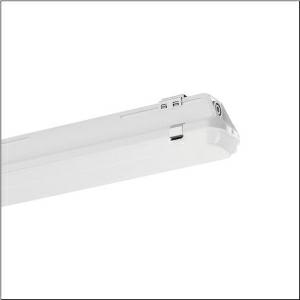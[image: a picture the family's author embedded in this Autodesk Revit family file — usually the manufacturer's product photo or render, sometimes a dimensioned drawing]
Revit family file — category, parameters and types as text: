
# Revit family: monsun_r__11_51fp107p430h_5718
name_source: partatom
category: Lighting Fixtures
units: mm (PartAtom-declared; Revit-internal decimal feet)

## family parameters
Cut with Voids When Loaded = No
Host = Face
Light Source = No
Part Type = Normal
Room Calculation Point = No
Round Connector Dimension = Use Diameter
Shared = No

## types (1)
- Monsun® 11 (1 x LED, 3970 lm, 22.2 W, 4000K)
    Apparent Load = 22 VA
    CIE Flux Codes = 47 77 93 94 100
    Color Rendering = 80
    Color Temperature = 4000K
    Default Elevation = 1800 mm
    Description = Monsun® 11, damp-proof luminaire, chain hanger, primary optical cover: enclosure, of PMMA, light emission: direct distribution, primary light characteristic: symmetric, installation type: suspended mounting, surface-mounted, horizontal mounting, vertical mounting, LED, rated luminous flux: 3.970lm, luminous efficacy: 179lm/W, light colour: 840, colour temperature: 4000K, control gear: ON/OFF, with terminal, 3-pole, max. 2.5mm², mains connection: 220..240V, AC, 50/60Hz, rated input power: 22W, luminaire housing, of glass-fibre reinforced polyester, uncoated, bright grey, incl. chain hanger, length: 1.590mm, width: 90mm, height: 88mm, clip for enclosure, of stainless steel (V2A), ceiling mounting element, of stainless steel (V2A), chain hanger, of stainless steel (V2A), protection rating (complete): IP66, insulation class (complete): insulation class I (protective earthing), certification: CE, ENEC, VDE, UKCA, protection symbol: D, impact resistance: IK04, permissible operating ambient temperature: -35..+40°C, standard: EN 50419, EN 60598-2-1, no direct snow, no direct sun, no direct rain, for indoor or canopied outdoor use, corresponds to IFS (International Featured Standards) requirements for safety and quality in the food industry, contact your sales advisor before using the luminaires in applications with unclear chemical exposure, large temperature fluctuations or condensation-forming humidity, LABS conformity tested according to VDMA 24364:2018-05, packaging unit: 1 piece
    Height = 89 mm
    Lamp = 1 x LED
    Lamp Light Flux = 3970 lm
    Lamp Power = 22.2 W
    Lamp count = 1
    Length = 1590 mm
    Luminous efficacy = 179 lm/W
    Manufacturer = Siteco
    ModVariant = No
    Model = 51FP107P430H
    Mounting Place = Ceiling
    Mounting Type = Surface mounted
    Number of Poles = 1
    OnlyDefault = Yes
    Power Factor = 1
    Product Name = Monsun® 11
    Product group = damp-proof luminaire
    ProductGroupID = 301
    Protection Class = Protection class I
    Protection Degree = IP 66
    RLX_Detail_Level = 1
    RLX_Emergency_Light_Flux = 0 lm
    RLX_Emergency_Type = 0
    RLX_Emergency_Type_DB = No
    RlxData = <blob elided: 88645 chars, md5=5bd7c426>
    Socket = socket
    Standby Power = 0 W
    System Light Flux = 3970 lm
    System Power = 22 W
    Type Comments = Product without accessories
    Type Image = l_1349237.jpg
    URL = http://relux.com
    VarID = ---
    Voltage = 0 V
    Weight = 0.00 kg
    Width = 90 mm

## geometry (parser evidence)
native form markers: Blend x4, Sweep x13
no freeform markers — native parametric forms only
